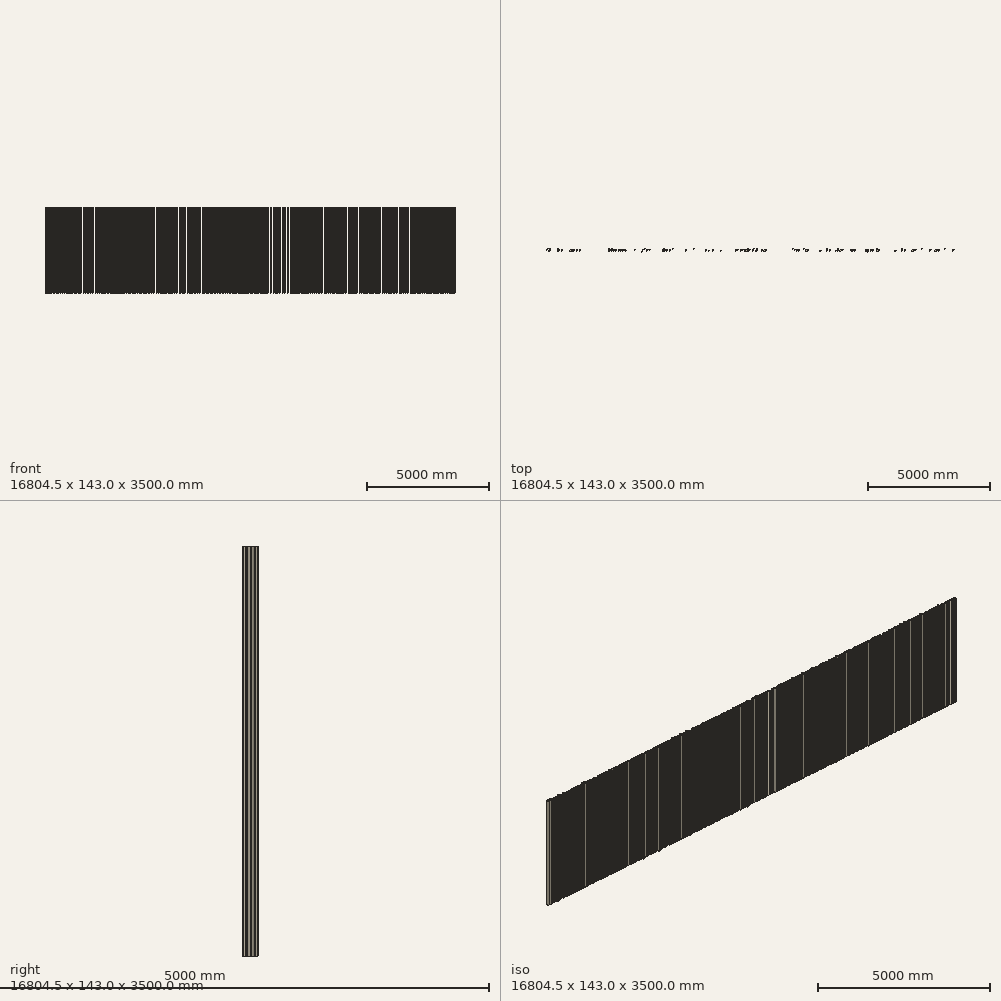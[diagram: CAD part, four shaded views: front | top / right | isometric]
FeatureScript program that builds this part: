
annotation { "Feature Type Name" : "Feature", "Feature Type Description" : "" }
export const myFeature = defineFeature(function(context is Context, id is Id, definition is map)
    precondition{}
    {
        {
            var Q0;
            Q0=qCreatedBy(makeId("Top.planeOp"),FACE);
            var sketch = newSketch(context, id + "F0", { "sketchPlane" : qUnion([Q0])});
            skText(sketch, "E0", { "text": "When, in the course of human events, it becomes necessary for one portion of the family of man to assume among the people of the earth a position different from that which they have hitherto occupied, but one to which the laws of nature and of nature", "fontName": "OpenSans-Regular.ttf"});
            const initialGuessF0  = {"E0": [-8.19743, -0.02675, 1, 0, 0.10242]};
            skSetInitialGuess(sketch, initialGuessF0);
            skSolve(sketch);
        }
        {
            var Q0;
            Q0 = qSketchRegion(id + "F0", true);
            extrude(context, id + "F1", {"entities" : qUnion([Q0]), "depth" : 3500 * mm, "offsetDistance" : 25 * mm});
        }
    });
